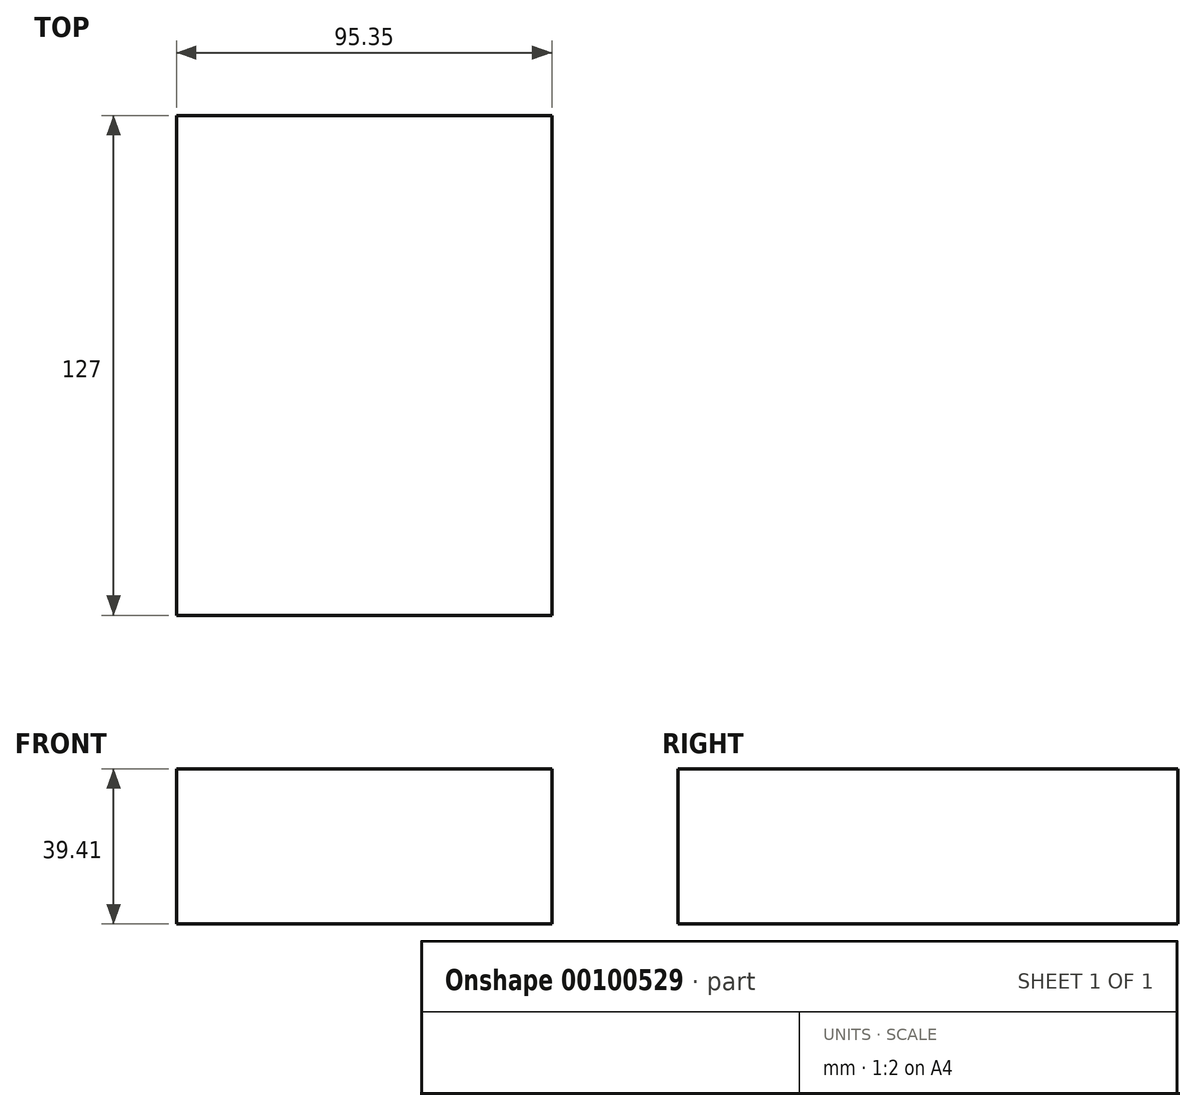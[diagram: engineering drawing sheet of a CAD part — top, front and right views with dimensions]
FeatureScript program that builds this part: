
annotation { "Feature Type Name" : "Feature", "Feature Type Description" : "" }
export const myFeature = defineFeature(function(context is Context, id is Id, definition is map)
    precondition{}
    {
        {
            var Q0;
            Q0=qCreatedBy(makeId("Front.planeOp"),FACE);
            var sketch = newSketch(context, id + "F0", { "sketchPlane" : qUnion([Q0])});
            skLineSegment(sketch, "E0.bottom", {"start": v(-56.16, -17.26) * mm, "end": v(39.19, -17.26) * mm});
            skLineSegment(sketch, "E0.top", {"start": v(-56.16, 22.15) * mm, "end": v(39.19, 22.15) * mm});
            skLineSegment(sketch, "E0.left", {"start": v(-56.16, -17.26) * mm, "end": v(-56.16, 22.15) * mm});
            skLineSegment(sketch, "E0.right", {"start": v(39.19, -17.26) * mm, "end": v(39.19, 22.15) * mm});
            skSolve(sketch);
        }
        {
            var Q0;
            Q0=makeQuery(id+"F0.imprint","IMPRINT",FACE,{"disambiguationData":[TD([[makeQuery(id+"F0.imprint","IMPRINT",EDGE,{"derivedFrom":sQuery(id+"F0.wireOp",EDGE,"E0.bottom")}),1.0]])]});
            extrude(context, id + "F1", {"entities" : qUnion([Q0]), "depth" : 127 * mm});
        }
    });
